# Revit family: 712-4920-001-DN100
name_source: partatom
category: Pipe Accessories
units: mm (PartAtom-declared; Revit-internal decimal feet)

## family parameters
Always vertical = Yes
Cut with Voids When Loaded = No
Part Type = Valve - Breaks Into
Round Connector Dimension = Use Diameter
Shared = No
Work Plane-Based = No

## types (1)
- DN100_PN10/16
    Body_wallthickness = 10 mm  [stored 0.0328084 ft]
    DN100_PN10/16 = 712-0100-49-201
    Description_ = AVK FLANGED PIPE W/LOOSE FLANGES
    FOD = 110 mm  [stored 0.360892 ft]
    Flange_thickness = 19 mm  [stored 0.062336 ft]
    ID(Radius) = 50 mm  [stored 0.164042 ft]
    L = 600 mm  [stored 1.9685 ft]
    Nominal Diameter (DN) = 100 mm  [stored 0.328084 ft]
    RF_Thick = 3 mm  [stored 0.00984252 ft]
    Rf_Dia = 78 mm  [stored 0.255906 ft]
    Search_Table = 712-4920-001-DN100
    URL product pages = https://www.avkvalves.com

note: [stored X ft] marks values corroborated as IEEE doubles in the binary element streams (Revit-internal decimal feet)

## geometry (parser evidence)
native form markers: Sweep x10
no freeform markers — native parametric forms only
